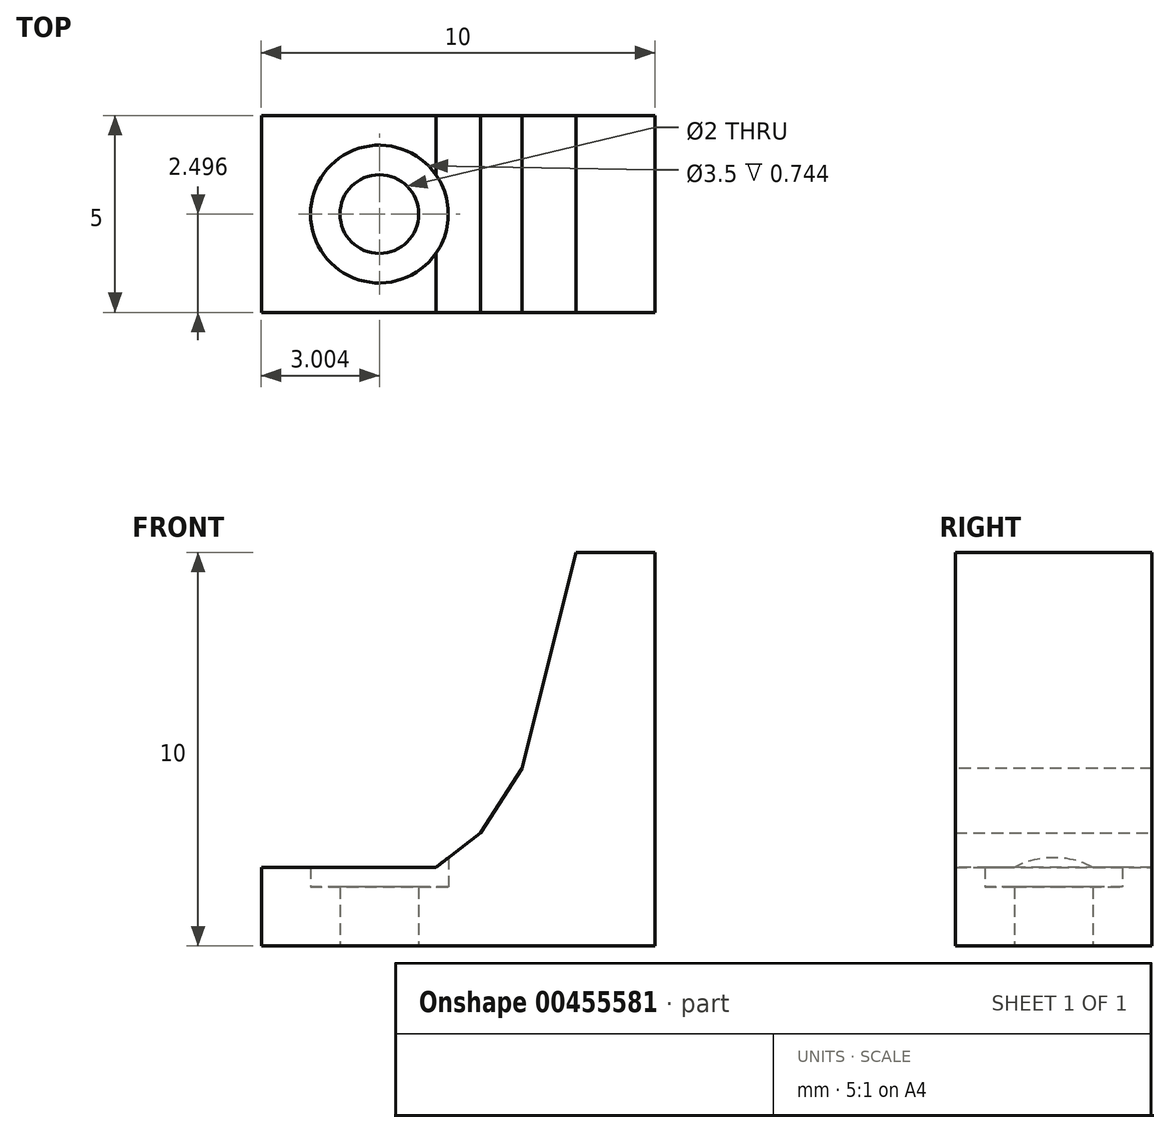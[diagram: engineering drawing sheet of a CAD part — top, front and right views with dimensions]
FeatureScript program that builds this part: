
annotation { "Feature Type Name" : "Feature", "Feature Type Description" : "" }
export const myFeature = defineFeature(function(context is Context, id is Id, definition is map)
    precondition{}
    {
        {
            var Q0;
            Q0=qCreatedBy(makeId("Top.planeOp"),FACE);
            var sketch = newSketch(context, id + "F0", { "sketchPlane" : qUnion([Q0])});
            skCircle(sketch, "E0", {"center": v(-50.9, 6.34) * mm, "radius": 1 * mm});
            skLineSegment(sketch, "E1", {"start": v(-63.33, 6.34) * mm, "end": v(-26.14, 6.34) * mm, "construction": true});
            skLineSegment(sketch, "E2.bottom", {"start": v(-47.9, 4.34) * mm, "end": v(-53.9, 4.34) * mm});
            skLineSegment(sketch, "E2.top", {"start": v(-47.9, 8.34) * mm, "end": v(-53.9, 8.34) * mm});
            skLineSegment(sketch, "E2.left", {"start": v(-47.9, 4.34) * mm, "end": v(-47.9, 8.34) * mm});
            skLineSegment(sketch, "E2.right", {"start": v(-53.9, 4.34) * mm, "end": v(-53.9, 8.34) * mm});
            skLineSegment(sketch, "E3.bottom", {"start": v(-47.9, 8.34) * mm, "end": v(-43.9, 8.34) * mm});
            skLineSegment(sketch, "E3.top", {"start": v(-47.9, 4.34) * mm, "end": v(-43.9, 4.34) * mm});
            skLineSegment(sketch, "E3.left", {"start": v(-47.9, 8.34) * mm, "end": v(-47.9, 4.34) * mm});
            skLineSegment(sketch, "E3.right", {"start": v(-43.9, 8.34) * mm, "end": v(-43.9, 4.34) * mm});
            skCircle(sketch, "E4", {"center": v(-50.9, 6.34) * mm, "radius": 1.75 * mm});
            skSolve(sketch);
        }
        {
            var Q0;
            Q0=sQuery(id+"F0.wireOp",EDGE,"E1");
            cPlane(context, id + "F1", {"entities" : qUnion([Q0]), "cplaneType" : CPlaneType.LINE_ANGLE, "offset" : 25 * mm, "angle" : 0 * degree, "width" : 150 * mm, "height" : 150 * mm});
        }
        {
            var Q0;
            Q0=qCreatedBy(id+"F1.planeOp",FACE);
            var sketch = newSketch(context, id + "F2", { "sketchPlane" : qUnion([Q0])});
            skLineSegment(sketch, "E5.0", {"start": v(47.9, 0) * mm, "end": v(53.9, 0) * mm});
            skLineSegment(sketch, "E5.1", {"start": v(47.9, 0) * mm, "end": v(43.9, 0) * mm});
            skLineSegment(sketch, "E6", {"start": v(43.9, 0) * mm, "end": v(56.7, 12.8) * mm, "construction": true});
            skLineSegment(sketch, "E7.MirrorCS", {"start": v(43.9, 4) * mm, "end": v(43.9, 10) * mm});
            skLineSegment(sketch, "E8.MirrorCS", {"start": v(43.9, 4) * mm, "end": v(43.9, 0) * mm});
            skLineSegment(sketch, "E9", {"start": v(53.9, 0) * mm, "end": v(53.9, 2) * mm});
            skLineSegment(sketch, "E10.MirrorCS", {"start": v(43.9, 10) * mm, "end": v(45.9, 10) * mm});
            skLineSegment(sketch, "E11", {"start": v(53.9, 2) * mm, "end": v(47.9, 2) * mm});
            skLineSegment(sketch, "E12", {"start": v(45.9, 10) * mm, "end": v(47.9, 2) * mm});
            skPoint(sketch, "E13.orphan", {"position": v(45.9, 2) * mm});
            skSolve(sketch);
        }
        {
            var Q0;
            Q0=makeQuery(id+"F2.imprint","IMPRINT",FACE,{"disambiguationData":[TD([[makeQuery(id+"F2.imprint","IMPRINT",EDGE,{"derivedFrom":sQuery(id+"F2.wireOp",EDGE,"E5.0")}),1.0]])]});
            extrude(context, id + "F3", {"entities" : qUnion([Q0]), "endBound" : BoundingType.SYMMETRIC, "depth" : 5 * mm, "offsetDistance" : 25 * mm});
        }
        {
            var Q0;
            Q0=makeQuery(id+"F0.imprint","IMPRINT",FACE,{"disambiguationData":[TD([[makeQuery(id+"F0.imprint","IMPRINT",EDGE,{"derivedFrom":sQuery(id+"F0.wireOp",EDGE,"E0")}),1.0]])]});
            extrude(context, id + "F4", {"entities" : qUnion([Q0]), "operationType" : NewBodyOperationType.REMOVE, "depth" : 25 * mm, "offsetDistance" : 25 * mm});
        }
        {
            var Q0;
            Q0=makeQuery(id+"F3.opExtrude","SWEPT_FACE",FACE,{"disambiguationData":[OSD([sQuery(id+"F2.wireOp",EDGE,"E7.MirrorCS"),sQuery(id+"F2.wireOp",EDGE,"E8.MirrorCS")])]});
            var sketch = newSketch(context, id + "F5", { "sketchPlane" : qUnion([Q0])});
            skLineSegment(sketch, "E14.0", {"start": v(8.84, 10) * mm, "end": v(3.84, 10) * mm, "construction": true});
            skLineSegment(sketch, "E14.1", {"start": v(8.84, 0) * mm, "end": v(8.84, 10) * mm, "construction": true});
            skLineSegment(sketch, "E15", {"start": v(6.34, 10) * mm, "end": v(6.34, 0) * mm, "construction": true});
            skCircle(sketch, "E16", {"center": v(6.34, 7) * mm, "radius": 1 * mm});
            skCircle(sketch, "E17", {"center": v(6.34, 7) * mm, "radius": 1.75 * mm});
            skSolve(sketch);
        }
        {
            var Q0;
            Q0=makeQuery(id+"F0.imprint","IMPRINT",FACE,{"disambiguationData":[TD([[makeQuery(id+"F0.imprint","IMPRINT",EDGE,{"derivedFrom":sQuery(id+"F0.wireOp",EDGE,"E0")}),-1.0]])]});
            extrude(context, id + "F6", {"entities" : qUnion([Q0]), "operationType" : NewBodyOperationType.REMOVE, "depth" : 10 * mm, "offsetDistance" : 25 * mm, "hasSecondDirection" : true, "secondDirectionOppositeDirection" : false, "secondDirectionDepth" : 1.5 * mm});
        }
        {
            var Q0;
            Q0=makeQuery(id+"F3.opExtrude","SWEPT_EDGE",EDGE,{"disambiguationData":[OSD([sQuery(id+"F2.wireOp",EDGE,"E11"),sQuery(id+"F2.wireOp",EDGE,"E12")])]});
            chamfer(context, id + "F7", {"entities" : qUnion([Q0]), "width" : 2 * mm, "tangentPropagation" : true});
        }
        {
            var Q0;
            {var subQ0=sQuery(id+"F2.wireOp",EDGE,"E12");Q0=makeQuery(id+"F7.opChamfer","BLEND_EDGE",EDGE,{"blendedFrom":[makeQuery(id+"F3.opExtrude","SWEPT_EDGE",EDGE,{"disambiguationData":[OSD([sQuery(id+"F2.wireOp",EDGE,"E11"),subQ0])]}),makeQuery(id+"F3.opExtrude","SWEPT_FACE",FACE,{"disambiguationData":[OSD([subQ0])]})],"blendedInto":[makeQuery(id+"F3.opExtrude","SWEPT_FACE",FACE,{"disambiguationData":[OSD([subQ0])]})]});}
            chamfer(context, id + "F8", {"entities" : qUnion([Q0]), "width" : 3 * mm, "tangentPropagation" : true});
        }
    });
